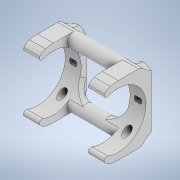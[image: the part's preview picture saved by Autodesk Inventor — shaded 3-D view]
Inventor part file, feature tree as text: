
AUTODESK INVENTOR PART (.ipt)
format: ipt  version: 2020 (Build 240168000, 168)  size: 677,888 bytes
history: native  units: mm
features: fillet x10, extrude x6, sketch x6, pattern_linear x1
ambient origin geometry x8: Origin, YZ Plane, XZ Plane, XY Plane, X Axis, Y Axis, Z Axis, Center Point
bodies: Solid1 (feature_tree)
feature tree (23):
  extrude  "Extrusion1"  Depth=2.5mm
  extrude  "Extrusion4"  Depth=26.0mm
  extrude  "Extrusion5"  Depth=0.85mm
  fillet  "Fillet2"  Radius=1.55mm
  fillet  "Fillet3"  Radius=1.8mm
  fillet  "Fillet4"  Radius=1.1mm
  fillet  "Fillet5"  Radius=21.0mm
  pattern_linear  "Rectangular Pattern1"  Spacing1=10.5mm  [1 undecoded]
  extrude  "Extrusion16"  Depth=3.5mm
  extrude  "Extrusion15"  Depth=4.0mm
  fillet  "Fillet16"  Radius=10.0mm
  extrude  "Extrusion17"  Depth=1.0mm
  fillet  "Fillet15"  Radius=0.1mm
  fillet  "Fillet11"  Radius=0.5mm
  fillet  "Fillet12"  Radius=3.6mm
  fillet  "Fillet13"  Radius=20.0mm
  fillet  "Fillet14"  Radius=5.0mm
  sketch  "Sketch1"  dims[d0=2.5mm d1=2.5mm]
  sketch  "Sketch6"  dims[d2=16.5mm d3=26.0mm]
  sketch  "Sketch7"  dims[d4=6.0mm d5=0.85mm d6=1.55mm d7=1.8mm d8=1.1mm d9=21.0mm d10=0.0mm]
  sketch  "Sketch22"  dims[d25=21.0mm]
  sketch  "Sketch23"  dims[d26=2.0mm]
  sketch  "Sketch24"  dims[d27=10.0mm d28=0.0mm d32=10.5mm d33=3.5mm d34=4.0mm d35=10.0mm d36=0.0mm d37=1.0mm d39=0.1mm d40=0.5mm d41=3.6mm d42=20.0mm d44=24.5mm d100=5.0mm d101=5.0mm d102=24.5mm d103=0.0mm d104=4.835mm d105=0.0mm d106=2.0mm d107=2.0mm d108=2.0mm d109=2.0mm d110=2.0mm d111=6.0mm d112=0.0mm d113=5.0mm d114=10.0mm d115=0.0mm d51=0.5mm d52=0.872665mm d53=0.5mm d54=0.872665mm d86=0.5mm d87=0.872665mm d88=0.5mm d89=0.872665mm d96=0.5mm d97=0.872665mm d98=0.5mm d99=0.872665mm]
note: 1 required parameter value undecoded (feature->parameter linkage not recoverable at this tier; creation-order binding heuristic only, values carry confidence <= 0.55)
